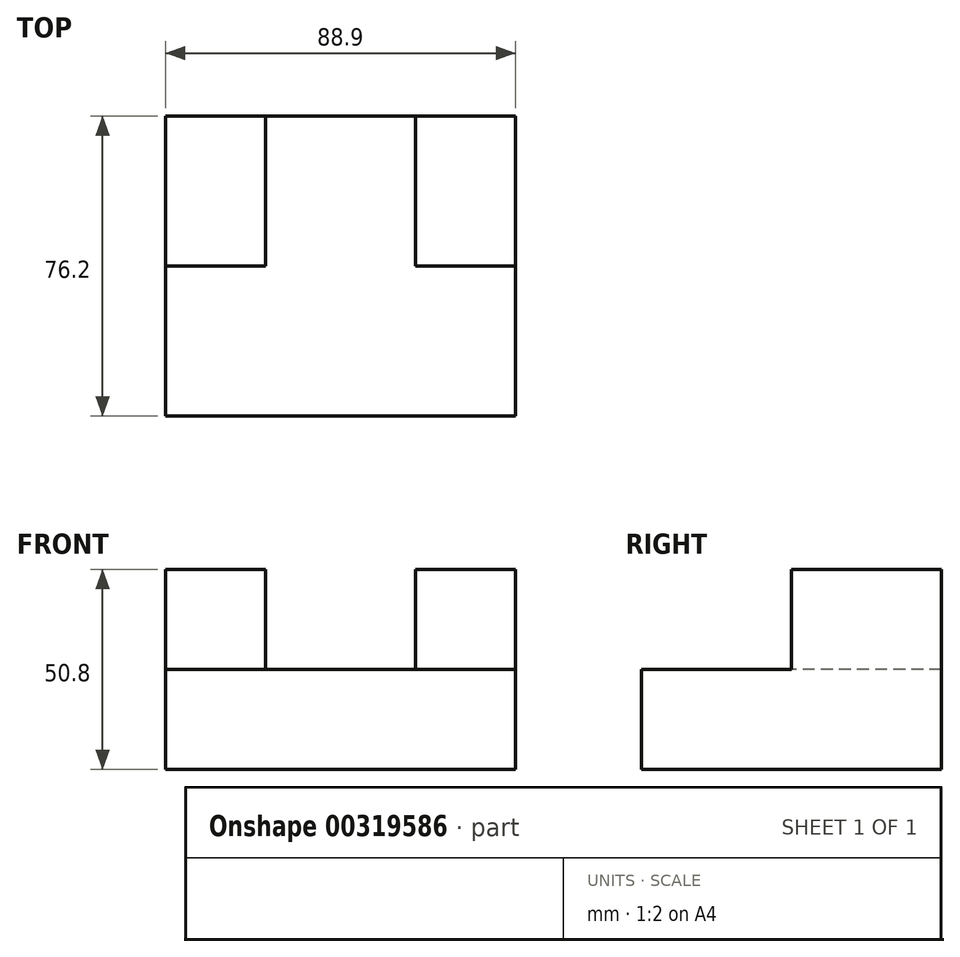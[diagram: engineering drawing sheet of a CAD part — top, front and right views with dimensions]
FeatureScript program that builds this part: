
annotation { "Feature Type Name" : "Feature", "Feature Type Description" : "" }
export const myFeature = defineFeature(function(context is Context, id is Id, definition is map)
    precondition{}
    {
        {
            var Q0;
            Q0=qCreatedBy(makeId("Front.planeOp"),FACE);
            var sketch = newSketch(context, id + "F0", { "sketchPlane" : qUnion([Q0])});
            skLineSegment(sketch, "E0", {"start": v(-44.9, -45.29) * mm, "end": v(44, -45.29) * mm});
            skLineSegment(sketch, "E1", {"start": v(-44.9, -45.29) * mm, "end": v(-44.9, -19.89) * mm});
            skLineSegment(sketch, "E2", {"start": v(-44.9, -19.89) * mm, "end": v(44, -19.89) * mm});
            skLineSegment(sketch, "E3", {"start": v(44, -19.89) * mm, "end": v(44, -45.29) * mm});
            skSolve(sketch);
        }
        {
            var Q0;
            Q0=makeQuery(id+"F0.imprint","IMPRINT",FACE,{"disambiguationData":[TD([[makeQuery(id+"F0.imprint","IMPRINT",EDGE,{"derivedFrom":sQuery(id+"F0.wireOp",EDGE,"E0")}),1.0]])]});
            extrude(context, id + "F1", {"entities" : qUnion([Q0]), "depth" : 76.2 * mm});
        }
        {
            var Q0;
            Q0=makeQuery(id+"F1.opExtrude","SWEPT_FACE",FACE,{"disambiguationData":[OSD([sQuery(id+"F0.wireOp",EDGE,"E2")])]});
            var sketch = newSketch(context, id + "F2", { "sketchPlane" : qUnion([Q0])});
            skLineSegment(sketch, "E4", {"start": v(44, 0) * mm, "end": v(18.6, 0) * mm});
            skLineSegment(sketch, "E5", {"start": v(18.6, 0) * mm, "end": v(18.6, -38.1) * mm});
            skLineSegment(sketch, "E6", {"start": v(18.6, -38.1) * mm, "end": v(44, -38.1) * mm});
            skLineSegment(sketch, "E7", {"start": v(44, -38.1) * mm, "end": v(44, 0) * mm});
            skLineSegment(sketch, "E8", {"start": v(-44.9, 0) * mm, "end": v(-19.5, 0) * mm});
            skLineSegment(sketch, "E9", {"start": v(-19.5, 0) * mm, "end": v(-19.5, -38.1) * mm});
            skLineSegment(sketch, "E10", {"start": v(-19.5, -38.1) * mm, "end": v(-44.9, -38.1) * mm});
            skLineSegment(sketch, "E11", {"start": v(-44.9, -38.1) * mm, "end": v(-44.9, 0) * mm});
            skSolve(sketch);
        }
        {
            var Q0;
            Q0=makeQuery(id+"F2.imprint","IMPRINT",FACE,{"disambiguationData":[TD([[makeQuery(id+"F2.imprint","IMPRINT",EDGE,{"derivedFrom":sQuery(id+"F2.wireOp",EDGE,"E4")}),-1.0]])]});
            var Q1;
            Q1=makeQuery(id+"F2.imprint","IMPRINT",FACE,{"disambiguationData":[TD([[makeQuery(id+"F2.imprint","IMPRINT",EDGE,{"derivedFrom":sQuery(id+"F2.wireOp",EDGE,"E8")}),-1.0]])]});
            extrude(context, id + "F3", {"entities" : qUnion([Q0, Q1]), "operationType" : NewBodyOperationType.ADD, "depth" : 25.4 * mm});
        }
    });
